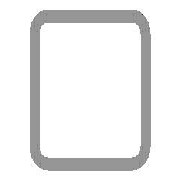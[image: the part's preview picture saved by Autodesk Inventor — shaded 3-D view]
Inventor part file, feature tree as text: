
AUTODESK INVENTOR PART (.ipt)
format: ipt  version: 2025 (Build 290162010, 162A)  size: 131,072 bytes
history: native  units: mm (DEFAULTED — no unit token found)
features: other x3, sketch x1, plane x1
ambient origin geometry x8: Origin, YZ Plane, XZ Plane, XY Plane, X Axis, Y Axis, Z Axis, Center Point
bodies: Solid1 (feature_tree), Body (feature_tree)
feature tree (5):
  other  "Driven Length"
  other  "Start plane"
  other  "End plane"
  sketch  "Sketch3"  dims[d3=2940.0mm d4=0.0mm d7=4.0mm d9=40.0mm d11=40.0mm d12=2.0mm d13=-0.0mm d14=2940.0mm d15=20.0mm d16=20.0mm d17=90.0deg d18=2940.0mm]
  plane  "Work Plane3"
